# Revit family: AFX-Lock_Pendant
name_source: partatom
category: Lighting Fixtures
units: mm (PartAtom-declared; Revit-internal decimal feet)

## family parameters
Cut with Voids When Loaded = No
Host = Face
Light Source = Yes
Part Type = Normal
Room Calculation Point = No
Round Connector Dimension = Use Diameter
Shared = No

## types (1)
- LCKP09L30D1BK
    Apparent Load = 0 VA
    Assembly Code = D5020200
    Cable Finish = AFX - Black Steel
    Color Filter = 16777215
    Colour Rendering Index = 90
    Default Elevation = 48"
    Description = Inter-twining spheres LED pendant with Adjustable cord 9 Ft - 9" Diameter x 9"H
    Diameter = 9"
    Diffuser Finish = AFX - White Acrylic
    Dimming Lamp Color Temperature Shift = <None>
    Frame Finish = AFX - Black Steel
    Height = 9"
    Housing Finish = AFX - Black Steel
    Keynote = 12500
    Manufacturer = AFX Inc
    Model = LCKP09L30D1BK
    Photometric Web File = PRLS0418L30D1XX.IES
    Product Documentation Link = https://www.afxinc.com
    Revit File Built By = https://servex-us.com
    Support Finish = AFX - Black Steel
    Tilt Angle = 0.00°
    Type Comments = Lock
    URL = https://www.afxinc.com
    Voltage = 120 V
    Wattage Comments = 20

## geometry (parser evidence)
native form markers: Sweep x2
no freeform markers — native parametric forms only
